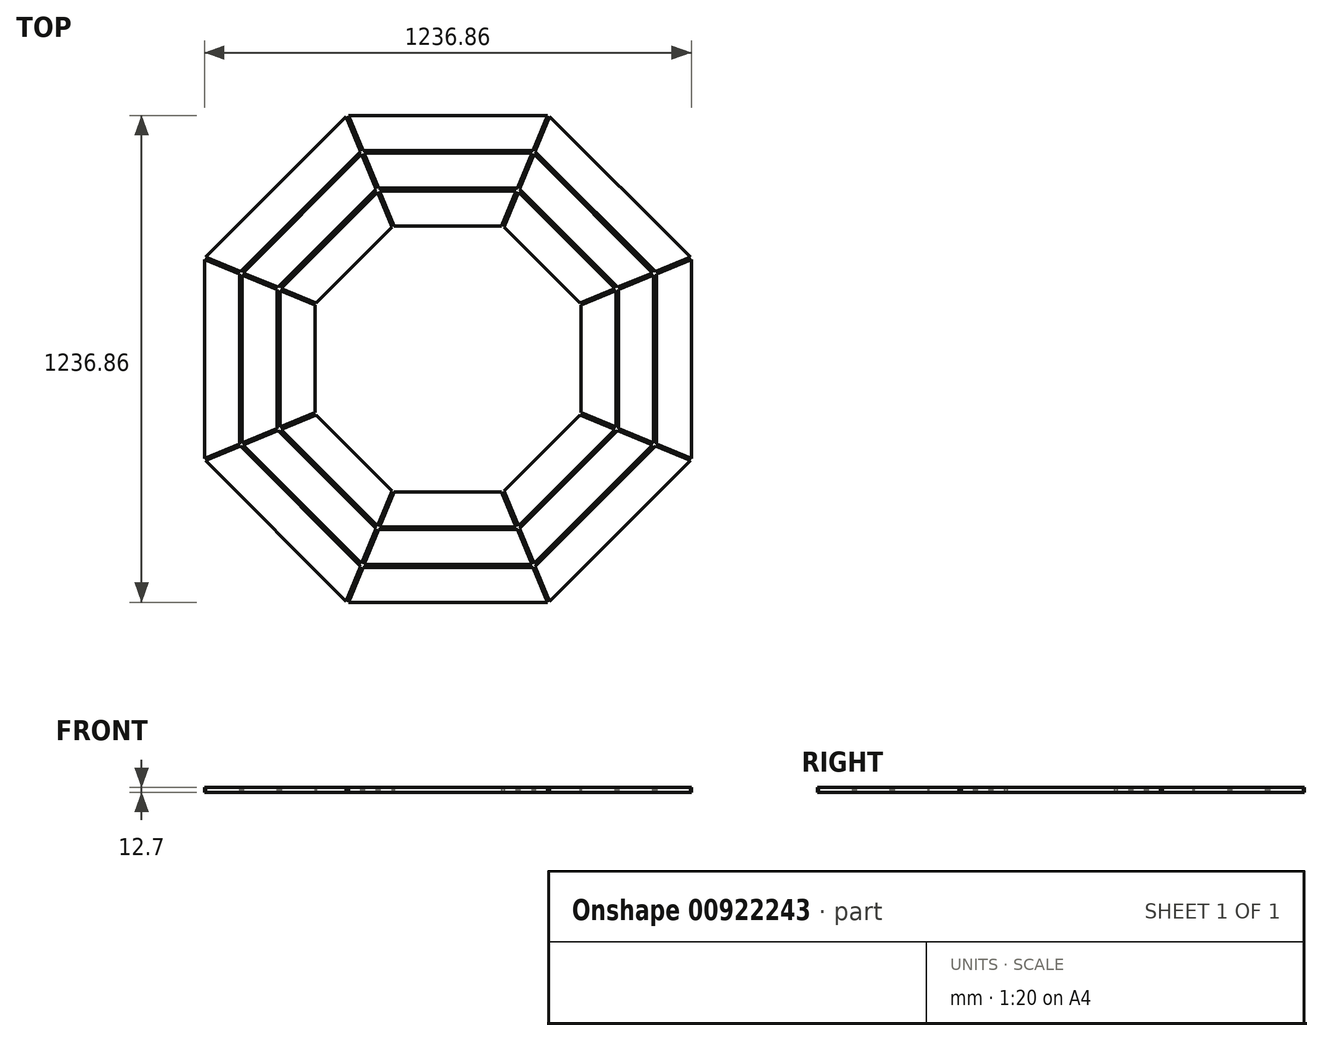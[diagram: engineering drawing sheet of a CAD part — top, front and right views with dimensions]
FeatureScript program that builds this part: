
annotation { "Feature Type Name" : "Feature", "Feature Type Description" : "" }
export const myFeature = defineFeature(function(context is Context, id is Id, definition is map)
    precondition{}
    {
        {
            var Q0;
            Q0=qCreatedBy(makeId("Top.planeOp"),FACE);
            var sketch = newSketch(context, id + "F0", { "sketchPlane" : qUnion([Q0])});
            skCircle(sketch, "E0", {"center": v(0, 0) * mm, "radius": 337.9 * mm, "construction": true});
            skLineSegment(sketch, "E1.6", {"start": v(-139.96, 337.9) * mm, "end": v(-136.53, 337.9) * mm, "construction": true});
            skPoint(sketch, "E1.0.midPoint", {"position": v(337.9, 0) * mm});
            skLineSegment(sketch, "E2.2", {"start": v(-176.79, 426.8) * mm, "end": v(-173.35, 426.8) * mm, "construction": true});
            skLineSegment(sketch, "E3", {"start": v(139.96, 337.9) * mm, "end": v(176.79, 426.8) * mm, "construction": true});
            skLineSegment(sketch, "E4", {"start": v(136.53, 337.9) * mm, "end": v(173.35, 426.8) * mm});
            skLineSegment(sketch, "E5.MirrorCS", {"start": v(142.4, 335.47) * mm, "end": v(179.22, 424.37) * mm, "construction": true});
            skLineSegment(sketch, "E6", {"start": v(0, 0) * mm, "end": v(139.96, 337.9) * mm, "construction": true});
            skLineSegment(sketch, "E7", {"start": v(-176.79, 426.8) * mm, "end": v(-139.96, 337.9) * mm, "construction": true});
            skLineSegment(sketch, "E8", {"start": v(-139.96, 337.9) * mm, "end": v(0, 0) * mm, "construction": true});
            skLineSegment(sketch, "E9", {"start": v(0, 0) * mm, "end": v(0, 337.9) * mm, "construction": true});
            skLineSegment(sketch, "E10.MirrorCS", {"start": v(-136.52, 337.9) * mm, "end": v(-173.35, 426.8) * mm});
            skLineSegment(sketch, "E11", {"start": v(-173.35, 426.8) * mm, "end": v(173.35, 426.8) * mm});
            skLineSegment(sketch, "E12", {"start": v(-136.53, 337.9) * mm, "end": v(136.53, 337.9) * mm});
            skLineSegment(sketch, "E13", {"start": v(136.53, 337.9) * mm, "end": v(139.96, 337.9) * mm, "construction": true});
            skLineSegment(sketch, "E14", {"start": v(173.35, 426.8) * mm, "end": v(176.79, 426.8) * mm, "construction": true});
            skLineSegment(sketch, "E15.1.0", {"start": v(-424.37, 179.22) * mm, "end": v(-179.22, 424.37) * mm});
            skLineSegment(sketch, "E15.1.1", {"start": v(-335.47, 142.4) * mm, "end": v(-142.4, 335.47) * mm});
            skLineSegment(sketch, "E15.1.2", {"start": v(-335.47, 142.4) * mm, "end": v(-424.37, 179.22) * mm});
            skLineSegment(sketch, "E15.1.3", {"start": v(-142.4, 335.47) * mm, "end": v(-179.22, 424.37) * mm});
            skLineSegment(sketch, "E15.2.0", {"start": v(-426.8, -173.35) * mm, "end": v(-426.8, 173.35) * mm});
            skLineSegment(sketch, "E15.2.1", {"start": v(-337.9, -136.52) * mm, "end": v(-337.9, 136.53) * mm});
            skLineSegment(sketch, "E15.2.2", {"start": v(-337.9, -136.52) * mm, "end": v(-426.8, -173.35) * mm});
            skLineSegment(sketch, "E15.2.3", {"start": v(-337.9, 136.53) * mm, "end": v(-426.8, 173.35) * mm});
            skLineSegment(sketch, "E15.3.0", {"start": v(-179.22, -424.37) * mm, "end": v(-424.37, -179.22) * mm});
            skLineSegment(sketch, "E15.3.1", {"start": v(-142.4, -335.47) * mm, "end": v(-335.47, -142.4) * mm});
            skLineSegment(sketch, "E15.3.2", {"start": v(-142.4, -335.47) * mm, "end": v(-179.22, -424.37) * mm});
            skLineSegment(sketch, "E15.3.3", {"start": v(-335.47, -142.4) * mm, "end": v(-424.37, -179.22) * mm});
            skLineSegment(sketch, "E15.4.0", {"start": v(173.35, -426.8) * mm, "end": v(-173.35, -426.8) * mm});
            skLineSegment(sketch, "E15.4.1", {"start": v(136.52, -337.9) * mm, "end": v(-136.53, -337.9) * mm});
            skLineSegment(sketch, "E15.4.2", {"start": v(136.52, -337.9) * mm, "end": v(173.35, -426.8) * mm});
            skLineSegment(sketch, "E15.4.3", {"start": v(-136.53, -337.9) * mm, "end": v(-173.35, -426.8) * mm});
            skLineSegment(sketch, "E15.5.0", {"start": v(424.37, -179.22) * mm, "end": v(179.22, -424.37) * mm});
            skLineSegment(sketch, "E15.5.1", {"start": v(335.47, -142.4) * mm, "end": v(142.4, -335.47) * mm});
            skLineSegment(sketch, "E15.5.2", {"start": v(335.47, -142.4) * mm, "end": v(424.37, -179.22) * mm});
            skLineSegment(sketch, "E15.5.3", {"start": v(142.4, -335.47) * mm, "end": v(179.22, -424.37) * mm});
            skLineSegment(sketch, "E15.6.0", {"start": v(426.8, 173.35) * mm, "end": v(426.8, -173.35) * mm});
            skLineSegment(sketch, "E15.6.1", {"start": v(337.9, 136.52) * mm, "end": v(337.9, -136.53) * mm});
            skLineSegment(sketch, "E15.6.2", {"start": v(337.9, 136.52) * mm, "end": v(426.8, 173.35) * mm});
            skLineSegment(sketch, "E15.6.3", {"start": v(337.9, -136.53) * mm, "end": v(426.8, -173.35) * mm});
            skLineSegment(sketch, "E15.7.0", {"start": v(179.22, 424.37) * mm, "end": v(424.37, 179.22) * mm});
            skLineSegment(sketch, "E15.7.1", {"start": v(142.4, 335.47) * mm, "end": v(335.47, 142.4) * mm});
            skLineSegment(sketch, "E15.7.2", {"start": v(142.4, 335.47) * mm, "end": v(179.22, 424.37) * mm});
            skLineSegment(sketch, "E15.7.3", {"start": v(335.47, 142.4) * mm, "end": v(424.37, 179.22) * mm});
            skSolve(sketch);
        }
        {
            var Q0;
            Q0 = qSketchRegion(id + "F0", true);
            extrude(context, id + "F1", {"entities" : qUnion([Q0]), "depth" : 12.7 * mm, "offsetDistance" : 25.4 * mm});
        }
        {
            var Q0;
            Q0=qCreatedBy(makeId("Top.planeOp"),FACE);
            var sketch = newSketch(context, id + "F2", { "sketchPlane" : qUnion([Q0])});
            skLineSegment(sketch, "E16", {"start": v(-213.04, 522.61) * mm, "end": v(213.04, 522.61) * mm});
            skLineSegment(sketch, "E17", {"start": v(213.04, 522.61) * mm, "end": v(176.21, 433.71) * mm});
            skLineSegment(sketch, "E18", {"start": v(176.21, 433.71) * mm, "end": v(-176.21, 433.71) * mm});
            skLineSegment(sketch, "E19", {"start": v(-176.21, 433.71) * mm, "end": v(-213.04, 522.61) * mm});
            skLineSegment(sketch, "E20.0.0", {"start": v(-173.35, 426.8) * mm, "end": v(-136.53, 337.9) * mm, "construction": true});
            skLineSegment(sketch, "E20.0.1", {"start": v(-136.52, 337.9) * mm, "end": v(136.53, 337.9) * mm, "construction": true});
            skLineSegment(sketch, "E20.0.2", {"start": v(136.52, 337.9) * mm, "end": v(173.35, 426.8) * mm, "construction": true});
            skLineSegment(sketch, "E20.0.3", {"start": v(173.35, 426.8) * mm, "end": v(-173.35, 426.8) * mm, "construction": true});
            skLineSegment(sketch, "E21", {"start": v(0, 337.9) * mm, "end": v(0, 426.8) * mm, "construction": true});
            skLineSegment(sketch, "E22", {"start": v(0, 433.71) * mm, "end": v(0, 522.61) * mm, "construction": true});
            skLineSegment(sketch, "E23.1.0", {"start": v(-431.28, 182.08) * mm, "end": v(-520.18, 218.9) * mm});
            skLineSegment(sketch, "E23.1.1", {"start": v(-520.18, 218.9) * mm, "end": v(-218.9, 520.18) * mm});
            skLineSegment(sketch, "E23.1.2", {"start": v(-218.9, 520.18) * mm, "end": v(-182.08, 431.28) * mm});
            skLineSegment(sketch, "E23.1.3", {"start": v(-182.08, 431.28) * mm, "end": v(-431.28, 182.08) * mm});
            skLineSegment(sketch, "E23.2.0", {"start": v(-433.71, -176.21) * mm, "end": v(-522.61, -213.04) * mm});
            skLineSegment(sketch, "E23.2.1", {"start": v(-522.61, -213.04) * mm, "end": v(-522.61, 213.04) * mm});
            skLineSegment(sketch, "E23.2.2", {"start": v(-522.61, 213.04) * mm, "end": v(-433.71, 176.21) * mm});
            skLineSegment(sketch, "E23.2.3", {"start": v(-433.71, 176.21) * mm, "end": v(-433.71, -176.21) * mm});
            skLineSegment(sketch, "E23.3.0", {"start": v(-182.08, -431.28) * mm, "end": v(-218.9, -520.18) * mm});
            skLineSegment(sketch, "E23.3.1", {"start": v(-218.9, -520.18) * mm, "end": v(-520.18, -218.9) * mm});
            skLineSegment(sketch, "E23.3.2", {"start": v(-520.18, -218.9) * mm, "end": v(-431.28, -182.08) * mm});
            skLineSegment(sketch, "E23.3.3", {"start": v(-431.28, -182.08) * mm, "end": v(-182.08, -431.28) * mm});
            skLineSegment(sketch, "E23.4.0", {"start": v(176.21, -433.71) * mm, "end": v(213.04, -522.61) * mm});
            skLineSegment(sketch, "E23.4.1", {"start": v(213.04, -522.61) * mm, "end": v(-213.04, -522.61) * mm});
            skLineSegment(sketch, "E23.4.2", {"start": v(-213.04, -522.61) * mm, "end": v(-176.21, -433.71) * mm});
            skLineSegment(sketch, "E23.4.3", {"start": v(-176.21, -433.71) * mm, "end": v(176.21, -433.71) * mm});
            skLineSegment(sketch, "E23.5.0", {"start": v(431.28, -182.08) * mm, "end": v(520.18, -218.9) * mm});
            skLineSegment(sketch, "E23.5.1", {"start": v(520.18, -218.9) * mm, "end": v(218.9, -520.18) * mm});
            skLineSegment(sketch, "E23.5.2", {"start": v(218.9, -520.18) * mm, "end": v(182.08, -431.28) * mm});
            skLineSegment(sketch, "E23.5.3", {"start": v(182.08, -431.28) * mm, "end": v(431.28, -182.08) * mm});
            skLineSegment(sketch, "E23.6.0", {"start": v(433.71, 176.21) * mm, "end": v(522.61, 213.04) * mm});
            skLineSegment(sketch, "E23.6.1", {"start": v(522.61, 213.04) * mm, "end": v(522.61, -213.04) * mm});
            skLineSegment(sketch, "E23.6.2", {"start": v(522.61, -213.04) * mm, "end": v(433.71, -176.21) * mm});
            skLineSegment(sketch, "E23.6.3", {"start": v(433.71, -176.21) * mm, "end": v(433.71, 176.21) * mm});
            skLineSegment(sketch, "E23.7.0", {"start": v(182.08, 431.28) * mm, "end": v(218.9, 520.18) * mm});
            skLineSegment(sketch, "E23.7.1", {"start": v(218.9, 520.18) * mm, "end": v(520.18, 218.9) * mm});
            skLineSegment(sketch, "E23.7.2", {"start": v(520.18, 218.9) * mm, "end": v(431.28, 182.08) * mm});
            skLineSegment(sketch, "E23.7.3", {"start": v(431.28, 182.08) * mm, "end": v(182.08, 431.28) * mm});
            skPoint(sketch, "E23.center", {"position": v(0, 0) * mm});
            skSolve(sketch);
        }
        {
            var Q0;
            Q0 = qSketchRegion(id + "F2", true);
            extrude(context, id + "F3", {"entities" : qUnion([Q0]), "depth" : 12.7 * mm, "offsetDistance" : 25.4 * mm});
        }
        {
            var Q0;
            Q0=qCreatedBy(makeId("Top.planeOp"),FACE);
            var sketch = newSketch(context, id + "F4", { "sketchPlane" : qUnion([Q0])});
            skLineSegment(sketch, "E24.0.0", {"start": v(-173.35, 426.8) * mm, "end": v(-136.53, 337.9) * mm, "construction": true});
            skLineSegment(sketch, "E24.0.1", {"start": v(-136.52, 337.9) * mm, "end": v(136.53, 337.9) * mm, "construction": true});
            skLineSegment(sketch, "E24.0.2", {"start": v(136.52, 337.9) * mm, "end": v(173.35, 426.8) * mm, "construction": true});
            skLineSegment(sketch, "E24.0.3", {"start": v(173.35, 426.8) * mm, "end": v(-173.35, 426.8) * mm, "construction": true});
            skLineSegment(sketch, "E25", {"start": v(0, 337.9) * mm, "end": v(0, 426.8) * mm, "construction": true});
            skLineSegment(sketch, "E26", {"start": v(-252.72, 618.43) * mm, "end": v(252.72, 618.43) * mm});
            skLineSegment(sketch, "E27", {"start": v(252.72, 618.43) * mm, "end": v(215.9, 529.53) * mm});
            skLineSegment(sketch, "E28", {"start": v(215.9, 529.53) * mm, "end": v(-215.9, 529.53) * mm});
            skLineSegment(sketch, "E29", {"start": v(-215.9, 529.53) * mm, "end": v(-252.72, 618.43) * mm});
            skLineSegment(sketch, "E30", {"start": v(0, 529.53) * mm, "end": v(0, 618.43) * mm, "construction": true});
            skLineSegment(sketch, "E31.1.0", {"start": v(-527.1, 221.77) * mm, "end": v(-616, 258.6) * mm});
            skLineSegment(sketch, "E31.1.1", {"start": v(-258.6, 616) * mm, "end": v(-221.77, 527.1) * mm});
            skLineSegment(sketch, "E31.1.2", {"start": v(-221.77, 527.1) * mm, "end": v(-527.1, 221.77) * mm});
            skLineSegment(sketch, "E31.1.3", {"start": v(-616, 258.6) * mm, "end": v(-258.6, 616) * mm});
            skLineSegment(sketch, "E31.2.0", {"start": v(-529.53, -215.9) * mm, "end": v(-618.43, -252.72) * mm});
            skLineSegment(sketch, "E31.2.1", {"start": v(-618.43, 252.72) * mm, "end": v(-529.53, 215.9) * mm});
            skLineSegment(sketch, "E31.2.2", {"start": v(-529.53, 215.9) * mm, "end": v(-529.53, -215.9) * mm});
            skLineSegment(sketch, "E31.2.3", {"start": v(-618.43, -252.72) * mm, "end": v(-618.43, 252.72) * mm});
            skLineSegment(sketch, "E31.3.0", {"start": v(-221.77, -527.1) * mm, "end": v(-258.6, -616) * mm});
            skLineSegment(sketch, "E31.3.1", {"start": v(-616, -258.6) * mm, "end": v(-527.1, -221.77) * mm});
            skLineSegment(sketch, "E31.3.2", {"start": v(-527.1, -221.77) * mm, "end": v(-221.77, -527.1) * mm});
            skLineSegment(sketch, "E31.3.3", {"start": v(-258.6, -616) * mm, "end": v(-616, -258.6) * mm});
            skLineSegment(sketch, "E31.4.0", {"start": v(215.9, -529.53) * mm, "end": v(252.72, -618.43) * mm});
            skLineSegment(sketch, "E31.4.1", {"start": v(-252.72, -618.43) * mm, "end": v(-215.9, -529.53) * mm});
            skLineSegment(sketch, "E31.4.2", {"start": v(-215.9, -529.53) * mm, "end": v(215.9, -529.53) * mm});
            skLineSegment(sketch, "E31.4.3", {"start": v(252.72, -618.43) * mm, "end": v(-252.72, -618.43) * mm});
            skLineSegment(sketch, "E31.5.0", {"start": v(527.1, -221.77) * mm, "end": v(616, -258.6) * mm});
            skLineSegment(sketch, "E31.5.1", {"start": v(258.6, -616) * mm, "end": v(221.77, -527.1) * mm});
            skLineSegment(sketch, "E31.5.2", {"start": v(221.77, -527.1) * mm, "end": v(527.1, -221.77) * mm});
            skLineSegment(sketch, "E31.5.3", {"start": v(616, -258.6) * mm, "end": v(258.6, -616) * mm});
            skLineSegment(sketch, "E31.6.0", {"start": v(529.53, 215.9) * mm, "end": v(618.43, 252.72) * mm});
            skLineSegment(sketch, "E31.6.1", {"start": v(618.43, -252.72) * mm, "end": v(529.53, -215.9) * mm});
            skLineSegment(sketch, "E31.6.2", {"start": v(529.53, -215.9) * mm, "end": v(529.53, 215.9) * mm});
            skLineSegment(sketch, "E31.6.3", {"start": v(618.43, 252.72) * mm, "end": v(618.43, -252.72) * mm});
            skLineSegment(sketch, "E31.7.0", {"start": v(221.77, 527.1) * mm, "end": v(258.6, 616) * mm});
            skLineSegment(sketch, "E31.7.1", {"start": v(616, 258.6) * mm, "end": v(527.1, 221.77) * mm});
            skLineSegment(sketch, "E31.7.2", {"start": v(527.1, 221.77) * mm, "end": v(221.77, 527.1) * mm});
            skLineSegment(sketch, "E31.7.3", {"start": v(258.6, 616) * mm, "end": v(616, 258.6) * mm});
            skPoint(sketch, "E31.center", {"position": v(0, 0) * mm});
            skSolve(sketch);
        }
        {
            var Q0;
            Q0 = qSketchRegion(id + "F4", true);
            extrude(context, id + "F5", {"entities" : qUnion([Q0]), "depth" : 12.7 * mm, "offsetDistance" : 25.4 * mm});
        }
    });
